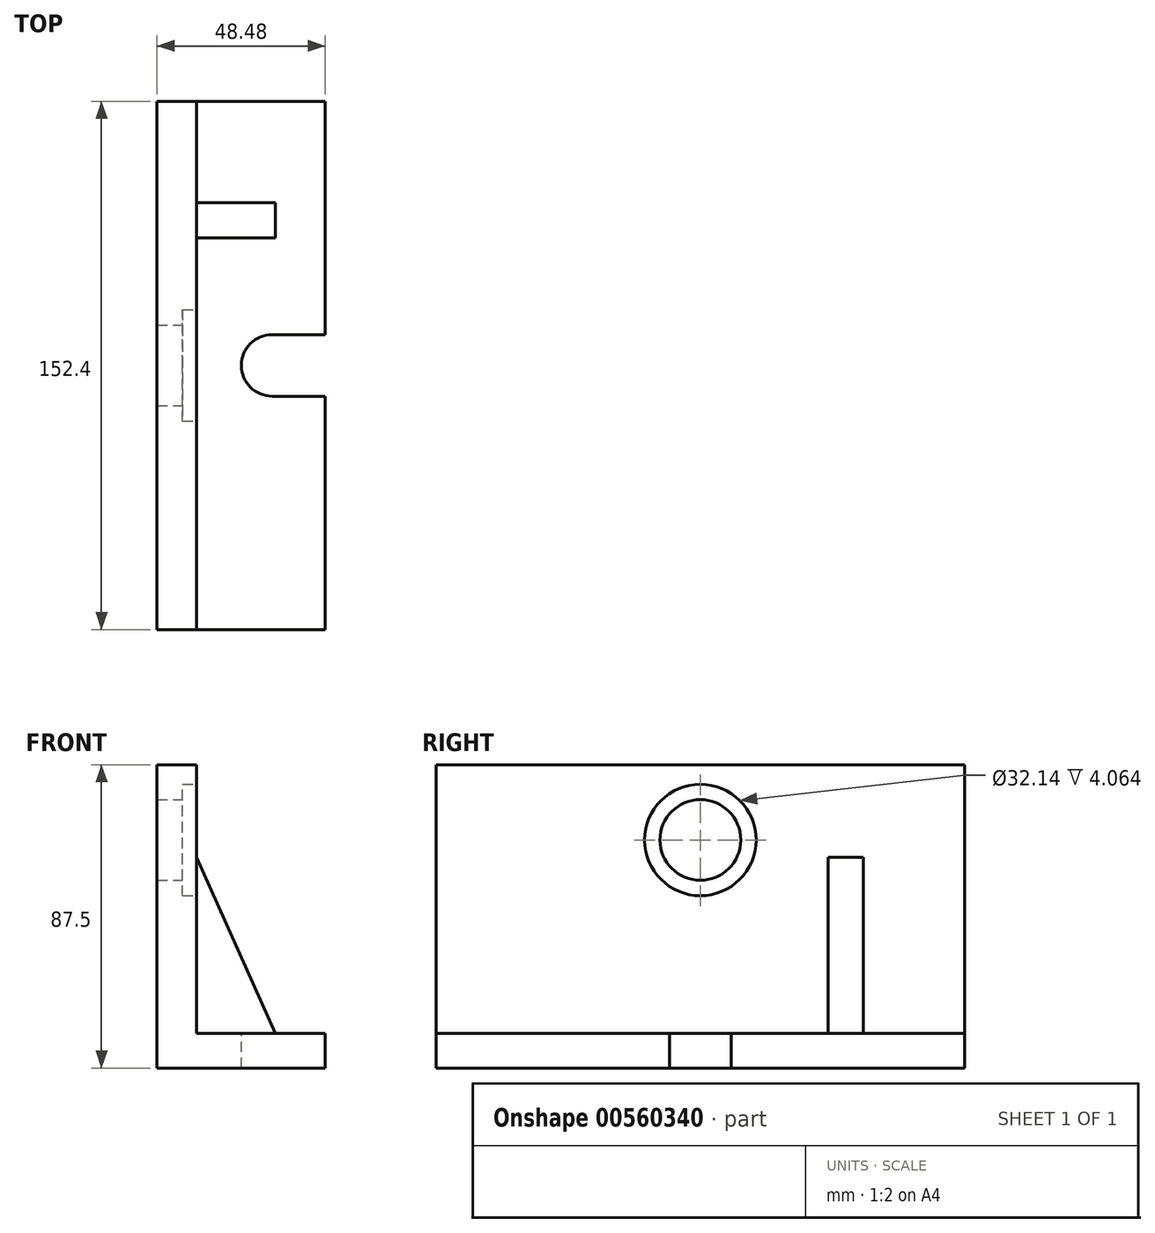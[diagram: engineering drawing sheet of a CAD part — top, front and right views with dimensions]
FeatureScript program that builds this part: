
annotation { "Feature Type Name" : "Feature", "Feature Type Description" : "" }
export const myFeature = defineFeature(function(context is Context, id is Id, definition is map)
    precondition{}
    {
        {
            var Q0;
            Q0=qCreatedBy(makeId("Front.planeOp"),FACE);
            var sketch = newSketch(context, id + "F0", { "sketchPlane" : qUnion([Q0])});
            skLineSegment(sketch, "E0", {"start": v(-46.9, 50.06) * mm, "end": v(-46.9, -27.4) * mm});
            skLineSegment(sketch, "E1", {"start": v(-46.9, -27.4) * mm, "end": v(-9.85, -27.4) * mm});
            skLineSegment(sketch, "E2", {"start": v(-9.85, -27.4) * mm, "end": v(-9.85, -37.44) * mm});
            skLineSegment(sketch, "E3", {"start": v(-9.85, -37.44) * mm, "end": v(-58.33, -37.44) * mm});
            skLineSegment(sketch, "E4", {"start": v(-58.33, -37.44) * mm, "end": v(-58.33, 50.06) * mm});
            skLineSegment(sketch, "E5", {"start": v(-46.9, 50.06) * mm, "end": v(-58.33, 50.06) * mm});
            skSolve(sketch);
        }
        {
            var Q0;
            Q0=makeQuery(id+"F0.imprint","IMPRINT",FACE,{"disambiguationData":[TD([[makeQuery(id+"F0.imprint","IMPRINT",EDGE,{"derivedFrom":sQuery(id+"F0.wireOp",EDGE,"E0")}),-1.0]])]});
            extrude(context, id + "F1", {"entities" : qUnion([Q0]), "endBound" : BoundingType.SYMMETRIC, "depth" : 152.4 * mm, "offsetDistance" : 25.4 * mm});
        }
        {
            var Q0;
            Q0=makeQuery(id+"F1.opExtrude","SWEPT_FACE",FACE,{"disambiguationData":[OSD([sQuery(id+"F0.wireOp",EDGE,"E0")])]});
            var sketch = newSketch(context, id + "F2", { "sketchPlane" : qUnion([Q0])});
            skCircle(sketch, "E6", {"center": v(0, 28.34) * mm, "radius": 11.64 * mm});
            skPoint(sketch, "E6.centerSnap0", {"position": v(0, 50.06) * mm});
            skSolve(sketch);
        }
        {
            var Q0;
            Q0 = qSketchRegion(id + "F2", true);
            extrude(context, id + "F3", {"entities" : qUnion([Q0]), "operationType" : NewBodyOperationType.REMOVE, "endBound" : BoundingType.SYMMETRIC, "oppositeDirection" : true, "depth" : 25.4 * mm, "offsetDistance" : 25.4 * mm});
        }
        {
            var Q0;
            Q0=makeQuery(id+"F1.opExtrude","SWEPT_FACE",FACE,{"disambiguationData":[OSD([sQuery(id+"F0.wireOp",EDGE,"E0")])]});
            var sketch = newSketch(context, id + "F4", { "sketchPlane" : qUnion([Q0])});
            skCircle(sketch, "E7", {"center": v(0, 28.34) * mm, "radius": 16.07 * mm});
            skSolve(sketch);
        }
        {
            var Q0;
            Q0=makeQuery(id+"F4.imprint","IMPRINT",FACE,{"disambiguationData":[TD([[makeQuery(id+"F4.imprint","IMPRINT",EDGE,{"derivedFrom":sQuery(id+"F4.wireOp",EDGE,"E7")}),1.0]])]});
            extrude(context, id + "F5", {"entities" : qUnion([Q0]), "operationType" : NewBodyOperationType.REMOVE, "oppositeDirection" : true, "depth" : 4.06 * mm, "offsetDistance" : 25.4 * mm});
        }
        {
            var Q0;
            Q0=makeQuery(id+"F1.opExtrude","SWEPT_FACE",FACE,{"disambiguationData":[OSD([sQuery(id+"F0.wireOp",EDGE,"E1")])]});
            var sketch = newSketch(context, id + "F6", { "sketchPlane" : qUnion([Q0])});
            skCircle(sketch, "E8", {"center": v(-25.1, 0) * mm, "radius": 8.9 * mm});
            skLineSegment(sketch, "E9", {"start": v(-25.1, 8.89) * mm, "end": v(-9.85, 8.89) * mm});
            skLineSegment(sketch, "E10", {"start": v(-25.1, -8.9) * mm, "end": v(-9.85, -8.9) * mm});
            skSolve(sketch);
        }
        {
            var Q0;
            Q0 = qSketchRegion(id + "F6", true);
            var Q1;
            {var subQ0=sQuery(id+"F6.wireOp",EDGE,"E9");Q1=makeQuery(id+"F6.imprint","IMPRINT",FACE,{"disambiguationData":[TD([[makeQuery(id+"F6.imprint","IMPRINT",EDGE,{"derivedFrom":subQ0}),-1.0]])]});}
            extrude(context, id + "F7", {"entities" : qUnion([Q0, Q1]), "operationType" : NewBodyOperationType.REMOVE, "endBound" : BoundingType.THROUGH_ALL, "oppositeDirection" : true, "depth" : 25.4 * mm, "offsetDistance" : 25.4 * mm});
        }
        {
            var Q0;
            Q0=qCreatedBy(makeId("Front.planeOp"),FACE);
            cPlane(context, id + "F8", {"entities" : qUnion([Q0]), "cplaneType" : CPlaneType.OFFSET, "offset" : 47 * mm, "oppositeDirection" : true, "width" : 152.4 * mm, "height" : 152.4 * mm});
        }
        {
            var Q0;
            Q0=qCreatedBy(id+"F8.planeOp",FACE);
            var sketch = newSketch(context, id + "F9", { "sketchPlane" : qUnion([Q0])});
            skLineSegment(sketch, "E11.0", {"start": v(-46.9, 23.4) * mm, "end": v(-46.9, -27.4) * mm});
            skLineSegment(sketch, "E12.0", {"start": v(-46.9, -27.4) * mm, "end": v(-24.26, -27.4) * mm});
            skLineSegment(sketch, "E13", {"start": v(-46.9, 23.4) * mm, "end": v(-24.26, -27.4) * mm});
            skSolve(sketch);
        }
        {
            var Q0;
            Q0 = qSketchRegion(id + "F9", true);
            extrude(context, id + "F10", {"entities" : qUnion([Q0]), "operationType" : NewBodyOperationType.ADD, "depth" : 10.16 * mm, "offsetDistance" : 25.4 * mm});
        }
    });
